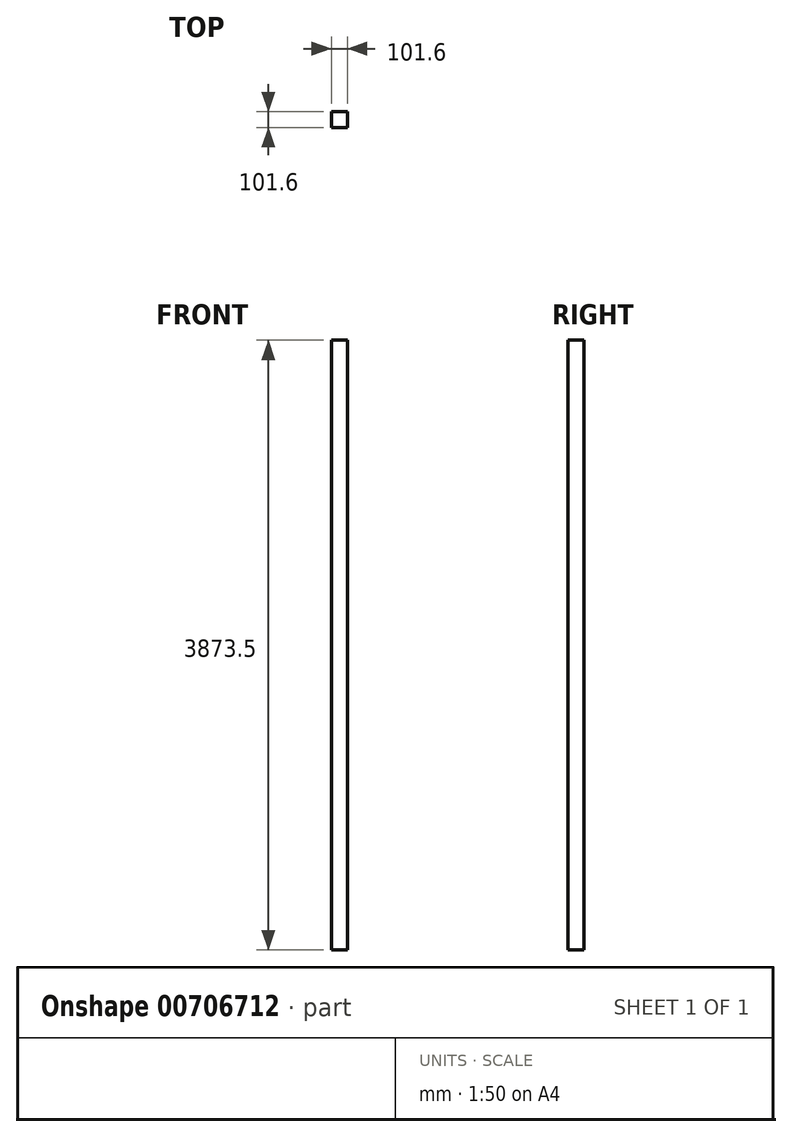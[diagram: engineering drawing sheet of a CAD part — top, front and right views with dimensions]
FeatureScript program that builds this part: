
annotation { "Feature Type Name" : "Feature", "Feature Type Description" : "" }
export const myFeature = defineFeature(function(context is Context, id is Id, definition is map)
    precondition{}
    {
        {
            var Q0;
            Q0=qCreatedBy(makeId("Front.planeOp"),FACE);
            var sketch = newSketch(context, id + "F0", { "sketchPlane" : qUnion([Q0])});
            skLineSegment(sketch, "E0.bottom", {"start": v(0, 0) * mm, "end": v(101.6, 0) * mm});
            skLineSegment(sketch, "E0.top", {"start": v(0, 3873.5) * mm, "end": v(101.6, 3873.5) * mm});
            skLineSegment(sketch, "E0.left", {"start": v(0, 0) * mm, "end": v(0, 3873.5) * mm});
            skLineSegment(sketch, "E0.right", {"start": v(101.6, 0) * mm, "end": v(101.6, 3873.5) * mm});
            skSolve(sketch);
        }
        {
            var Q0;
            Q0=makeQuery(id+"F0.imprint","IMPRINT",FACE,{"disambiguationData":[TD([[makeQuery(id+"F0.imprint","IMPRINT",EDGE,{"derivedFrom":sQuery(id+"F0.wireOp",EDGE,"E0.bottom")}),1.0]])]});
            extrude(context, id + "F1", {"entities" : qUnion([Q0]), "depth" : 101.6 * mm, "offsetDistance" : 25.4 * mm});
        }
    });
